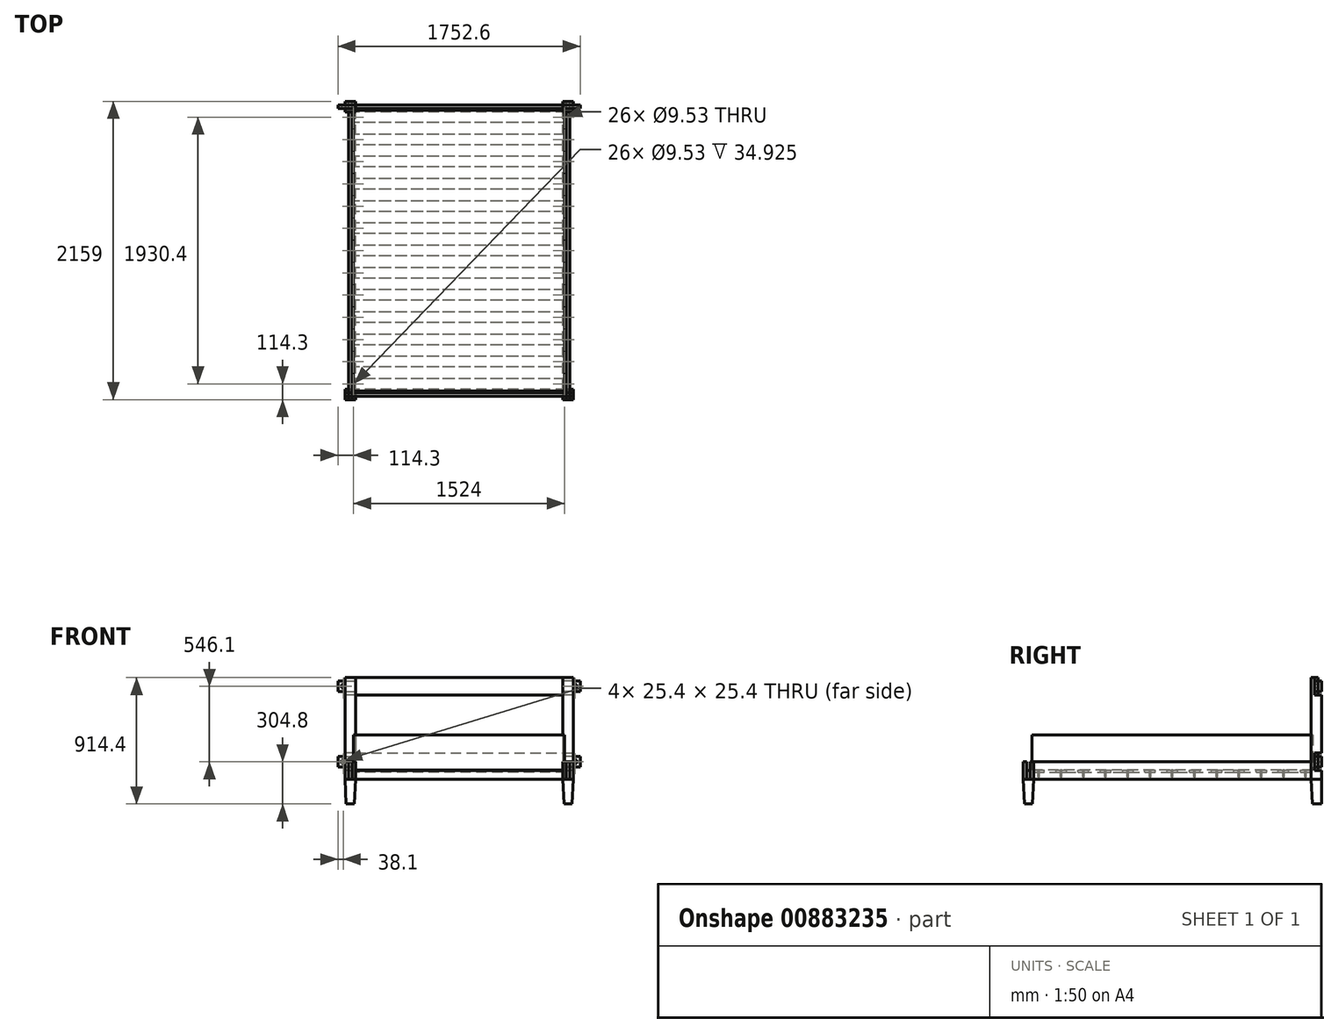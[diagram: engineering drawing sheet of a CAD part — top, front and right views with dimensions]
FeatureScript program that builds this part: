
annotation { "Feature Type Name" : "Feature", "Feature Type Description" : "" }
export const myFeature = defineFeature(function(context is Context, id is Id, definition is map)
    precondition{}
    {
        {
            var Q0;
            Q0=qCreatedBy(makeId("Top.planeOp"),FACE);
            var sketch = newSketch(context, id + "F0", { "sketchPlane" : qUnion([Q0])});
            skLineSegment(sketch, "E0.bottom", {"start": v(0, 0) * mm, "end": v(76.2, 0) * mm});
            skLineSegment(sketch, "E0.top", {"start": v(0, 76.2) * mm, "end": v(76.2, 76.2) * mm});
            skLineSegment(sketch, "E0.left", {"start": v(0, 0) * mm, "end": v(0, 76.2) * mm});
            skLineSegment(sketch, "E0.right", {"start": v(76.2, 0) * mm, "end": v(76.2, 76.2) * mm});
            skLineSegment(sketch, "E1.bottom", {"start": v(1574.8, 0) * mm, "end": v(1651, 0) * mm});
            skLineSegment(sketch, "E1.top", {"start": v(1574.8, 76.2) * mm, "end": v(1651, 76.2) * mm});
            skLineSegment(sketch, "E1.left", {"start": v(1574.8, 0) * mm, "end": v(1574.8, 76.2) * mm});
            skLineSegment(sketch, "E1.right", {"start": v(1651, 0) * mm, "end": v(1651, 76.2) * mm});
            skLineSegment(sketch, "E2.bottom", {"start": v(0, 2082.8) * mm, "end": v(76.2, 2082.8) * mm});
            skLineSegment(sketch, "E2.top", {"start": v(0, 2159) * mm, "end": v(76.2, 2159) * mm});
            skLineSegment(sketch, "E2.left", {"start": v(0, 2082.8) * mm, "end": v(0, 2159) * mm});
            skLineSegment(sketch, "E2.right", {"start": v(76.2, 2082.8) * mm, "end": v(76.2, 2159) * mm});
            skLineSegment(sketch, "E3.bottom", {"start": v(1574.8, 2082.8) * mm, "end": v(1651, 2082.8) * mm});
            skLineSegment(sketch, "E3.top", {"start": v(1574.8, 2159) * mm, "end": v(1651, 2159) * mm});
            skLineSegment(sketch, "E3.left", {"start": v(1574.8, 2082.8) * mm, "end": v(1574.8, 2159) * mm});
            skLineSegment(sketch, "E3.right", {"start": v(1651, 2082.8) * mm, "end": v(1651, 2159) * mm});
            skSolve(sketch);
        }
        {
            var Q0;
            Q0 = qSketchRegion(id + "F0", true);
            extrude(context, id + "F1", {"entities" : qUnion([Q0]), "depth" : 304.8 * mm, "offsetDistance" : 25.4 * mm});
        }
        {
            var Q0;
            Q0=makeQuery(id+"F1.opExtrude","CAP_FACE",FACE,{"disambiguationData":[OSD([sQuery(id+"F0.wireOp",EDGE,"E2.bottom"),sQuery(id+"F0.wireOp",EDGE,"E2.top"),sQuery(id+"F0.wireOp",EDGE,"E2.left"),sQuery(id+"F0.wireOp",EDGE,"E2.right")])],"isStart":false});
            var Q1;
            Q1=makeQuery(id+"F1.opExtrude","CAP_FACE",FACE,{"disambiguationData":[OSD([sQuery(id+"F0.wireOp",EDGE,"E3.bottom"),sQuery(id+"F0.wireOp",EDGE,"E3.top"),sQuery(id+"F0.wireOp",EDGE,"E3.left"),sQuery(id+"F0.wireOp",EDGE,"E3.right")])],"isStart":false});
            extrude(context, id + "F2", {"entities" : qUnion([Q0, Q1]), "operationType" : NewBodyOperationType.ADD, "depth" : 609.6 * mm, "offsetDistance" : 25.4 * mm});
        }
        {
            var Q0;
            {var subQ0=sQuery(id+"F0.wireOp",EDGE,"E2.top");Q0=makeQuery(id+"F2.boolean.opBoolean","MERGE",FACE,{"derivedFrom":[makeQuery(id+"F1.opExtrude","SWEPT_FACE",FACE,{"disambiguationData":[OSD([subQ0])]}),makeQuery(id+"F2.opExtrude","SWEPT_FACE",FACE,{"disambiguationData":[OSD([subQ0])]})]});}
            var sketch = newSketch(context, id + "F3", { "sketchPlane" : qUnion([Q0])});
            skLineSegment(sketch, "E4.bottom", {"start": v(-25.4, 304.8) * mm, "end": v(-50.8, 304.8) * mm});
            skLineSegment(sketch, "E4.top", {"start": v(-50.8, 177.8) * mm, "end": v(-25.4, 177.8) * mm});
            skLineSegment(sketch, "E4.left", {"start": v(-25.4, 304.8) * mm, "end": v(-25.4, 177.8) * mm});
            skLineSegment(sketch, "E4.right", {"start": v(-50.8, 304.8) * mm, "end": v(-50.8, 177.8) * mm});
            skLineSegment(sketch, "E5", {"start": v(-38.1, 177.8) * mm, "end": v(-38.1, 0) * mm, "construction": true});
            skPoint(sketch, "E5.endSnap0", {"position": v(-38.1, 0) * mm});
            skLineSegment(sketch, "E6.bottom", {"start": v(-1625.6, 304.8) * mm, "end": v(-1600.2, 304.8) * mm});
            skLineSegment(sketch, "E6.top", {"start": v(-1625.6, 177.8) * mm, "end": v(-1600.2, 177.8) * mm});
            skLineSegment(sketch, "E6.left", {"start": v(-1625.6, 304.8) * mm, "end": v(-1625.6, 177.8) * mm});
            skLineSegment(sketch, "E6.right", {"start": v(-1600.2, 304.8) * mm, "end": v(-1600.2, 177.8) * mm});
            skLineSegment(sketch, "E7", {"start": v(-1612.9, 177.8) * mm, "end": v(-1612.9, 0) * mm, "construction": true});
            skSolve(sketch);
        }
        {
            var Q0;
            Q0 = qSketchRegion(id + "F3", true);
            var Q1;
            Q1=makeQuery(id+"F1.opExtrude","SWEPT_FACE",FACE,{"disambiguationData":[OSD([sQuery(id+"F0.wireOp",EDGE,"E0.bottom")])]});
            extrude(context, id + "F4", {"entities" : qUnion([Q0]), "endBound" : BoundingType.UP_TO_SURFACE, "oppositeDirection" : true, "depth" : 25.4 * mm, "endBoundEntityFace" : qUnion([Q1]), "offsetDistance" : 25.4 * mm});
        }
        {
            var Q0;
            Q0=makeQuery(id+"F4.opExtrude","SWEPT_BODY",BODY,{"disambiguationData":[OSD([sQuery(id+"F3.wireOp",EDGE,"E4.bottom"),sQuery(id+"F3.wireOp",EDGE,"E4.top"),sQuery(id+"F3.wireOp",EDGE,"E4.left"),sQuery(id+"F3.wireOp",EDGE,"E4.right")])]});
            var Q1;
            Q1=makeQuery(id+"F4.opExtrude","SWEPT_BODY",BODY,{"disambiguationData":[OSD([sQuery(id+"F3.wireOp",EDGE,"E6.bottom"),sQuery(id+"F3.wireOp",EDGE,"E6.top"),sQuery(id+"F3.wireOp",EDGE,"E6.left"),sQuery(id+"F3.wireOp",EDGE,"E6.right")])]});
            var Q2;
            Q2=makeQuery(id+"F1.opExtrude","SWEPT_BODY",BODY,{"disambiguationData":[OSD([sQuery(id+"F0.wireOp",EDGE,"E0.bottom"),sQuery(id+"F0.wireOp",EDGE,"E0.top"),sQuery(id+"F0.wireOp",EDGE,"E0.left"),sQuery(id+"F0.wireOp",EDGE,"E0.right")])]});
            var Q3;
            Q3=makeQuery(id+"F1.opExtrude","SWEPT_BODY",BODY,{"disambiguationData":[OSD([sQuery(id+"F0.wireOp",EDGE,"E1.bottom"),sQuery(id+"F0.wireOp",EDGE,"E1.top"),sQuery(id+"F0.wireOp",EDGE,"E1.left"),sQuery(id+"F0.wireOp",EDGE,"E1.right")])]});
            booleanBodies(context, id + "F5", {"operationType" : BooleanOperationType.SUBTRACTION, "tools" : qUnion([Q0, Q1]), "targets" : qUnion([Q2, Q3]), "keepTools" : true});
        }
        {
            var Q0;
            Q0=makeQuery(id+"F1.opExtrude","SWEPT_FACE",FACE,{"disambiguationData":[OSD([sQuery(id+"F0.wireOp",EDGE,"E1.right")])]});
            var sketch = newSketch(context, id + "F6", { "sketchPlane" : qUnion([Q0])});
            skLineSegment(sketch, "E8.bottom", {"start": v(25.4, 304.8) * mm, "end": v(50.8, 304.8) * mm});
            skLineSegment(sketch, "E8.top", {"start": v(25.4, 177.8) * mm, "end": v(50.8, 177.8) * mm});
            skLineSegment(sketch, "E8.left", {"start": v(25.4, 304.8) * mm, "end": v(25.4, 177.8) * mm});
            skLineSegment(sketch, "E8.right", {"start": v(50.8, 304.8) * mm, "end": v(50.8, 177.8) * mm});
            skLineSegment(sketch, "E9", {"start": v(0, 304.8) * mm, "end": v(25.4, 304.8) * mm, "construction": true});
            skLineSegment(sketch, "E10", {"start": v(76.2, 304.8) * mm, "end": v(50.8, 304.8) * mm, "construction": true});
            skSolve(sketch);
        }
        {
            var Q0;
            Q0 = qSketchRegion(id + "F6", true);
            var Q1;
            Q1=makeQuery(id+"F1.opExtrude","SWEPT_FACE",FACE,{"disambiguationData":[OSD([sQuery(id+"F0.wireOp",EDGE,"E0.left")])]});
            extrude(context, id + "F7", {"entities" : qUnion([Q0]), "endBound" : BoundingType.UP_TO_SURFACE, "oppositeDirection" : true, "depth" : 25.4 * mm, "endBoundEntityFace" : qUnion([Q1]), "offsetDistance" : 25.4 * mm});
        }
        {
            var Q0;
            Q0=makeQuery(id+"F7.opExtrude","SWEPT_BODY",BODY,{"disambiguationData":[OSD([sQuery(id+"F6.wireOp",EDGE,"E8.bottom"),sQuery(id+"F6.wireOp",EDGE,"E8.top"),sQuery(id+"F6.wireOp",EDGE,"E8.left"),sQuery(id+"F6.wireOp",EDGE,"E8.right")])]});
            var Q1;
            Q1=makeQuery(id+"F1.opExtrude","SWEPT_BODY",BODY,{"disambiguationData":[OSD([sQuery(id+"F0.wireOp",EDGE,"E0.bottom"),sQuery(id+"F0.wireOp",EDGE,"E0.top"),sQuery(id+"F0.wireOp",EDGE,"E0.left"),sQuery(id+"F0.wireOp",EDGE,"E0.right")])]});
            var Q2;
            Q2=makeQuery(id+"F1.opExtrude","SWEPT_BODY",BODY,{"disambiguationData":[OSD([sQuery(id+"F0.wireOp",EDGE,"E1.bottom"),sQuery(id+"F0.wireOp",EDGE,"E1.top"),sQuery(id+"F0.wireOp",EDGE,"E1.left"),sQuery(id+"F0.wireOp",EDGE,"E1.right")])]});
            booleanBodies(context, id + "F8", {"operationType" : BooleanOperationType.SUBTRACTION, "tools" : qUnion([Q0]), "targets" : qUnion([Q1, Q2]), "keepTools" : true});
        }
        {
            var Q0;
            Q0=makeQuery(id+"F7.opExtrude","CAP_FACE",FACE,{"disambiguationData":[OSD([sQuery(id+"F6.wireOp",EDGE,"E8.bottom"),sQuery(id+"F6.wireOp",EDGE,"E8.top"),sQuery(id+"F6.wireOp",EDGE,"E8.left"),sQuery(id+"F6.wireOp",EDGE,"E8.right")])],"isStart":false});
            var sketch = newSketch(context, id + "F9", { "sketchPlane" : qUnion([Q0])});
            skLineSegment(sketch, "E11.bottom", {"start": v(-50.8, 304.8) * mm, "end": v(-25.4, 304.8) * mm});
            skLineSegment(sketch, "E11.top", {"start": v(-50.8, 241.3) * mm, "end": v(-25.4, 241.3) * mm});
            skLineSegment(sketch, "E11.left", {"start": v(-50.8, 304.8) * mm, "end": v(-50.8, 241.3) * mm});
            skLineSegment(sketch, "E11.right", {"start": v(-25.4, 304.8) * mm, "end": v(-25.4, 241.3) * mm});
            skSolve(sketch);
        }
        {
            var Q0;
            Q0 = qSketchRegion(id + "F9", true);
            extrude(context, id + "F10", {"entities" : qUnion([Q0]), "operationType" : NewBodyOperationType.REMOVE, "endBound" : BoundingType.THROUGH_ALL, "oppositeDirection" : true, "depth" : 25.4 * mm, "offsetDistance" : 25.4 * mm});
        }
        {
            var Q0;
            Q0=makeQuery(id+"F4.opExtrude","SWEPT_BODY",BODY,{"disambiguationData":[OSD([sQuery(id+"F3.wireOp",EDGE,"E4.bottom"),sQuery(id+"F3.wireOp",EDGE,"E4.top"),sQuery(id+"F3.wireOp",EDGE,"E4.left"),sQuery(id+"F3.wireOp",EDGE,"E4.right")])]});
            var Q1;
            Q1=makeQuery(id+"F4.opExtrude","SWEPT_BODY",BODY,{"disambiguationData":[OSD([sQuery(id+"F3.wireOp",EDGE,"E6.bottom"),sQuery(id+"F3.wireOp",EDGE,"E6.top"),sQuery(id+"F3.wireOp",EDGE,"E6.left"),sQuery(id+"F3.wireOp",EDGE,"E6.right")])]});
            var Q2;
            Q2=makeQuery(id+"F7.opExtrude","SWEPT_BODY",BODY,{"disambiguationData":[OSD([sQuery(id+"F6.wireOp",EDGE,"E8.bottom"),sQuery(id+"F6.wireOp",EDGE,"E8.top"),sQuery(id+"F6.wireOp",EDGE,"E8.left"),sQuery(id+"F6.wireOp",EDGE,"E8.right")])]});
            booleanBodies(context, id + "F11", {"operationType" : BooleanOperationType.SUBTRACTION, "tools" : qUnion([Q0, Q1]), "targets" : qUnion([Q2]), "keepTools" : true});
        }
        {
            var Q0;
            Q0=makeQuery(id+"F4.opExtrude","SWEPT_BODY",BODY,{"disambiguationData":[OSD([sQuery(id+"F3.wireOp",EDGE,"E4.bottom"),sQuery(id+"F3.wireOp",EDGE,"E4.top"),sQuery(id+"F3.wireOp",EDGE,"E4.left"),sQuery(id+"F3.wireOp",EDGE,"E4.right")])]});
            var Q1;
            Q1=makeQuery(id+"F4.opExtrude","SWEPT_BODY",BODY,{"disambiguationData":[OSD([sQuery(id+"F3.wireOp",EDGE,"E6.bottom"),sQuery(id+"F3.wireOp",EDGE,"E6.top"),sQuery(id+"F3.wireOp",EDGE,"E6.left"),sQuery(id+"F3.wireOp",EDGE,"E6.right")])]});
            var Q2;
            Q2=makeQuery(id+"F1.opExtrude","SWEPT_BODY",BODY,{"disambiguationData":[OSD([sQuery(id+"F0.wireOp",EDGE,"E2.bottom"),sQuery(id+"F0.wireOp",EDGE,"E2.top"),sQuery(id+"F0.wireOp",EDGE,"E2.left"),sQuery(id+"F0.wireOp",EDGE,"E2.right")])]});
            var Q3;
            Q3=makeQuery(id+"F1.opExtrude","SWEPT_BODY",BODY,{"disambiguationData":[OSD([sQuery(id+"F0.wireOp",EDGE,"E3.bottom"),sQuery(id+"F0.wireOp",EDGE,"E3.top"),sQuery(id+"F0.wireOp",EDGE,"E3.left"),sQuery(id+"F0.wireOp",EDGE,"E3.right")])]});
            booleanBodies(context, id + "F12", {"operationType" : BooleanOperationType.SUBTRACTION, "tools" : qUnion([Q0, Q1]), "targets" : qUnion([Q2, Q3]), "keepTools" : true});
        }
        {
            var Q0;
            {var subQ0=sQuery(id+"F0.wireOp",EDGE,"E2.left");Q0=makeQuery(id+"F2.boolean.opBoolean","MERGE",FACE,{"derivedFrom":[makeQuery(id+"F1.opExtrude","SWEPT_FACE",FACE,{"disambiguationData":[OSD([subQ0])]}),makeQuery(id+"F2.opExtrude","SWEPT_FACE",FACE,{"disambiguationData":[OSD([subQ0])]})]});}
            var sketch = newSketch(context, id + "F13", { "sketchPlane" : qUnion([Q0])});
            skLineSegment(sketch, "E12.bottom", {"start": v(-2133.6, 368.3) * mm, "end": v(-2108.2, 368.3) * mm});
            skLineSegment(sketch, "E12.top", {"start": v(-2133.6, 241.3) * mm, "end": v(-2108.2, 241.3) * mm});
            skLineSegment(sketch, "E12.left", {"start": v(-2133.6, 368.3) * mm, "end": v(-2133.6, 241.3) * mm});
            skLineSegment(sketch, "E12.right", {"start": v(-2108.2, 368.3) * mm, "end": v(-2108.2, 241.3) * mm});
            skLineSegment(sketch, "E13", {"start": v(-2159, 241.3) * mm, "end": v(-2133.6, 241.3) * mm});
            skLineSegment(sketch, "E14", {"start": v(-2082.8, 241.3) * mm, "end": v(-2108.2, 241.3) * mm});
            skLineSegment(sketch, "E15.bottom", {"start": v(-2133.6, 914.4) * mm, "end": v(-2108.2, 914.4) * mm});
            skLineSegment(sketch, "E15.top", {"start": v(-2133.6, 787.4) * mm, "end": v(-2108.2, 787.4) * mm});
            skLineSegment(sketch, "E15.left", {"start": v(-2133.6, 914.4) * mm, "end": v(-2133.6, 787.4) * mm});
            skLineSegment(sketch, "E15.right", {"start": v(-2108.2, 914.4) * mm, "end": v(-2108.2, 787.4) * mm});
            skSolve(sketch);
        }
        {
            var Q0;
            Q0 = qSketchRegion(id + "F13", true);
            extrude(context, id + "F14", {"entities" : qUnion([Q0]), "depth" : 50.8 * mm, "offsetDistance" : 25.4 * mm, "hasSecondDirection" : true, "secondDirectionOppositeDirection" : true, "secondDirectionDepth" : 1701.8 * mm});
        }
        {
            var Q0;
            Q0=makeQuery(id+"F14.opExtrude","SWEPT_FACE",FACE,{"disambiguationData":[OSD([sQuery(id+"F13.wireOp",EDGE,"E15.right")])]});
            var sketch = newSketch(context, id + "F15", { "sketchPlane" : qUnion([Q0])});
            skLineSegment(sketch, "E16.bottom", {"start": v(-50.8, 914.4) * mm, "end": v(76.2, 914.4) * mm});
            skLineSegment(sketch, "E16.top", {"start": v(-50.8, 889) * mm, "end": v(76.2, 889) * mm});
            skLineSegment(sketch, "E16.left", {"start": v(-50.8, 914.4) * mm, "end": v(-50.8, 889) * mm});
            skLineSegment(sketch, "E16.right", {"start": v(76.2, 914.4) * mm, "end": v(76.2, 889) * mm});
            skLineSegment(sketch, "E17.bottom", {"start": v(-50.8, 787.4) * mm, "end": v(76.2, 787.4) * mm});
            skLineSegment(sketch, "E17.top", {"start": v(-50.8, 812.8) * mm, "end": v(76.2, 812.8) * mm});
            skLineSegment(sketch, "E17.left", {"start": v(-50.8, 787.4) * mm, "end": v(-50.8, 812.8) * mm});
            skLineSegment(sketch, "E17.right", {"start": v(76.2, 787.4) * mm, "end": v(76.2, 812.8) * mm});
            skLineSegment(sketch, "E18.bottom", {"start": v(-50.8, 368.3) * mm, "end": v(76.2, 368.3) * mm});
            skLineSegment(sketch, "E18.top", {"start": v(-50.8, 342.9) * mm, "end": v(76.2, 342.9) * mm});
            skLineSegment(sketch, "E18.left", {"start": v(-50.8, 368.3) * mm, "end": v(-50.8, 342.9) * mm});
            skLineSegment(sketch, "E18.right", {"start": v(76.2, 368.3) * mm, "end": v(76.2, 342.9) * mm});
            skLineSegment(sketch, "E19.bottom", {"start": v(76.2, 241.3) * mm, "end": v(-50.8, 241.3) * mm});
            skLineSegment(sketch, "E19.top", {"start": v(76.2, 266.7) * mm, "end": v(-50.8, 266.7) * mm});
            skLineSegment(sketch, "E19.left", {"start": v(76.2, 241.3) * mm, "end": v(76.2, 266.7) * mm});
            skLineSegment(sketch, "E19.right", {"start": v(-50.8, 241.3) * mm, "end": v(-50.8, 266.7) * mm});
            skLineSegment(sketch, "E20.bottom", {"start": v(1701.8, 368.3) * mm, "end": v(1574.8, 368.3) * mm});
            skLineSegment(sketch, "E20.top", {"start": v(1701.8, 342.9) * mm, "end": v(1574.8, 342.9) * mm});
            skLineSegment(sketch, "E20.left", {"start": v(1701.8, 368.3) * mm, "end": v(1701.8, 342.9) * mm});
            skLineSegment(sketch, "E20.right", {"start": v(1574.8, 368.3) * mm, "end": v(1574.8, 342.9) * mm});
            skLineSegment(sketch, "E21.bottom", {"start": v(1701.8, 241.3) * mm, "end": v(1574.8, 241.3) * mm});
            skLineSegment(sketch, "E21.top", {"start": v(1701.8, 266.7) * mm, "end": v(1574.8, 266.7) * mm});
            skLineSegment(sketch, "E21.left", {"start": v(1701.8, 241.3) * mm, "end": v(1701.8, 266.7) * mm});
            skLineSegment(sketch, "E21.right", {"start": v(1574.8, 241.3) * mm, "end": v(1574.8, 266.7) * mm});
            skLineSegment(sketch, "E22.bottom", {"start": v(1701.8, 914.4) * mm, "end": v(1574.8, 914.4) * mm});
            skLineSegment(sketch, "E22.top", {"start": v(1701.8, 889) * mm, "end": v(1574.8, 889) * mm});
            skLineSegment(sketch, "E22.left", {"start": v(1701.8, 914.4) * mm, "end": v(1701.8, 889) * mm});
            skLineSegment(sketch, "E22.right", {"start": v(1574.8, 914.4) * mm, "end": v(1574.8, 889) * mm});
            skLineSegment(sketch, "E23.bottom", {"start": v(1701.8, 787.4) * mm, "end": v(1574.8, 787.4) * mm});
            skLineSegment(sketch, "E23.top", {"start": v(1701.8, 812.8) * mm, "end": v(1574.8, 812.8) * mm});
            skLineSegment(sketch, "E23.left", {"start": v(1701.8, 787.4) * mm, "end": v(1701.8, 812.8) * mm});
            skLineSegment(sketch, "E23.right", {"start": v(1574.8, 787.4) * mm, "end": v(1574.8, 812.8) * mm});
            skLineSegment(sketch, "E24.bottom", {"start": v(0, 838.2) * mm, "end": v(-25.4, 838.2) * mm});
            skLineSegment(sketch, "E24.top", {"start": v(0, 863.6) * mm, "end": v(-25.4, 863.6) * mm});
            skLineSegment(sketch, "E24.left", {"start": v(0, 838.2) * mm, "end": v(0, 863.6) * mm});
            skLineSegment(sketch, "E24.right", {"start": v(-25.4, 838.2) * mm, "end": v(-25.4, 863.6) * mm});
            skLineSegment(sketch, "E25", {"start": v(-50.8, 850.9) * mm, "end": v(-25.4, 850.9) * mm, "construction": true});
            skLineSegment(sketch, "E26.bottom", {"start": v(0, 292.1) * mm, "end": v(-25.4, 292.1) * mm});
            skLineSegment(sketch, "E26.top", {"start": v(0, 317.5) * mm, "end": v(-25.4, 317.5) * mm});
            skLineSegment(sketch, "E26.left", {"start": v(0, 292.1) * mm, "end": v(0, 317.5) * mm});
            skLineSegment(sketch, "E26.right", {"start": v(-25.4, 292.1) * mm, "end": v(-25.4, 317.5) * mm});
            skLineSegment(sketch, "E27", {"start": v(-50.8, 304.8) * mm, "end": v(-25.4, 304.8) * mm, "construction": true});
            skLineSegment(sketch, "E28.bottom", {"start": v(1651, 292.1) * mm, "end": v(1676.4, 292.1) * mm});
            skLineSegment(sketch, "E28.top", {"start": v(1651, 317.5) * mm, "end": v(1676.4, 317.5) * mm});
            skLineSegment(sketch, "E28.left", {"start": v(1651, 292.1) * mm, "end": v(1651, 317.5) * mm});
            skLineSegment(sketch, "E28.right", {"start": v(1676.4, 292.1) * mm, "end": v(1676.4, 317.5) * mm});
            skLineSegment(sketch, "E29", {"start": v(1676.4, 304.8) * mm, "end": v(1701.8, 304.8) * mm, "construction": true});
            skLineSegment(sketch, "E30.bottom", {"start": v(1651, 863.6) * mm, "end": v(1676.4, 863.6) * mm});
            skLineSegment(sketch, "E30.top", {"start": v(1651, 838.2) * mm, "end": v(1676.4, 838.2) * mm});
            skLineSegment(sketch, "E30.left", {"start": v(1651, 863.6) * mm, "end": v(1651, 838.2) * mm});
            skLineSegment(sketch, "E30.right", {"start": v(1676.4, 863.6) * mm, "end": v(1676.4, 838.2) * mm});
            skLineSegment(sketch, "E31", {"start": v(1676.4, 850.9) * mm, "end": v(1701.8, 850.9) * mm, "construction": true});
            skSolve(sketch);
        }
        {
            var Q0;
            Q0 = qSketchRegion(id + "F15", true);
            extrude(context, id + "F16", {"entities" : qUnion([Q0]), "operationType" : NewBodyOperationType.REMOVE, "endBound" : BoundingType.THROUGH_ALL, "oppositeDirection" : true, "depth" : 25.4 * mm, "offsetDistance" : 25.4 * mm});
        }
        {
            var Q0;
            Q0=makeQuery(id+"F14.opExtrude","SWEPT_BODY",BODY,{"disambiguationData":[OSD([sQuery(id+"F13.wireOp",EDGE,"E15.bottom"),sQuery(id+"F13.wireOp",EDGE,"E15.top"),sQuery(id+"F13.wireOp",EDGE,"E15.left"),sQuery(id+"F13.wireOp",EDGE,"E15.right")])]});
            var Q1;
            Q1=makeQuery(id+"F14.opExtrude","SWEPT_BODY",BODY,{"disambiguationData":[OSD([sQuery(id+"F13.wireOp",EDGE,"E12.bottom"),sQuery(id+"F13.wireOp",EDGE,"E12.top"),sQuery(id+"F13.wireOp",EDGE,"E12.left"),sQuery(id+"F13.wireOp",EDGE,"E12.right")])]});
            var Q2;
            Q2=makeQuery(id+"F1.opExtrude","SWEPT_BODY",BODY,{"disambiguationData":[OSD([sQuery(id+"F0.wireOp",EDGE,"E2.bottom"),sQuery(id+"F0.wireOp",EDGE,"E2.top"),sQuery(id+"F0.wireOp",EDGE,"E2.left"),sQuery(id+"F0.wireOp",EDGE,"E2.right")])]});
            var Q3;
            Q3=makeQuery(id+"F4.opExtrude","SWEPT_BODY",BODY,{"disambiguationData":[OSD([sQuery(id+"F3.wireOp",EDGE,"E4.bottom"),sQuery(id+"F3.wireOp",EDGE,"E4.top"),sQuery(id+"F3.wireOp",EDGE,"E4.left"),sQuery(id+"F3.wireOp",EDGE,"E4.right")])]});
            var Q4;
            Q4=makeQuery(id+"F4.opExtrude","SWEPT_BODY",BODY,{"disambiguationData":[OSD([sQuery(id+"F3.wireOp",EDGE,"E6.bottom"),sQuery(id+"F3.wireOp",EDGE,"E6.top"),sQuery(id+"F3.wireOp",EDGE,"E6.left"),sQuery(id+"F3.wireOp",EDGE,"E6.right")])]});
            var Q5;
            Q5=makeQuery(id+"F1.opExtrude","SWEPT_BODY",BODY,{"disambiguationData":[OSD([sQuery(id+"F0.wireOp",EDGE,"E3.bottom"),sQuery(id+"F0.wireOp",EDGE,"E3.top"),sQuery(id+"F0.wireOp",EDGE,"E3.left"),sQuery(id+"F0.wireOp",EDGE,"E3.right")])]});
            booleanBodies(context, id + "F17", {"operationType" : BooleanOperationType.SUBTRACTION, "tools" : qUnion([Q0, Q1]), "targets" : qUnion([Q2, Q3, Q4, Q5]), "keepTools" : true});
        }
        {
            var Q0;
            {var subQ0=sQuery(id+"F0.wireOp",EDGE,"E2.bottom");Q0=makeQuery(id+"F2.boolean.opBoolean","MERGE",FACE,{"derivedFrom":[makeQuery(id+"F1.opExtrude","SWEPT_FACE",FACE,{"disambiguationData":[OSD([subQ0])]}),makeQuery(id+"F2.opExtrude","SWEPT_FACE",FACE,{"disambiguationData":[OSD([subQ0])]})]});}
            var sketch = newSketch(context, id + "F18", { "sketchPlane" : qUnion([Q0])});
            skLineSegment(sketch, "E32.bottom", {"start": v(50.8, 177.8) * mm, "end": v(76.2, 177.8) * mm});
            skLineSegment(sketch, "E32.top", {"start": v(50.8, 228.6) * mm, "end": v(76.2, 228.6) * mm});
            skLineSegment(sketch, "E32.left", {"start": v(50.8, 177.8) * mm, "end": v(50.8, 228.6) * mm});
            skLineSegment(sketch, "E32.right", {"start": v(76.2, 177.8) * mm, "end": v(76.2, 228.6) * mm});
            skLineSegment(sketch, "E33.bottom", {"start": v(1600.2, 177.8) * mm, "end": v(1574.8, 177.8) * mm});
            skLineSegment(sketch, "E33.top", {"start": v(1600.2, 228.6) * mm, "end": v(1574.8, 228.6) * mm});
            skLineSegment(sketch, "E33.left", {"start": v(1600.2, 177.8) * mm, "end": v(1600.2, 228.6) * mm});
            skLineSegment(sketch, "E33.right", {"start": v(1574.8, 177.8) * mm, "end": v(1574.8, 228.6) * mm});
            skSolve(sketch);
        }
        {
            var Q0;
            Q0 = qSketchRegion(id + "F18", true);
            var Q1;
            Q1=makeQuery(id+"F1.opExtrude","SWEPT_FACE",FACE,{"disambiguationData":[OSD([sQuery(id+"F0.wireOp",EDGE,"E0.top")])]});
            extrude(context, id + "F19", {"entities" : qUnion([Q0]), "endBound" : BoundingType.UP_TO_SURFACE, "depth" : 25.4 * mm, "endBoundEntityFace" : qUnion([Q1]), "offsetDistance" : 25.4 * mm});
        }
        {
            var Q0;
            Q0=makeQuery(id+"F4.opExtrude","SWEPT_FACE",FACE,{"disambiguationData":[OSD([sQuery(id+"F3.wireOp",EDGE,"E4.right")])]});
            var sketch = newSketch(context, id + "F20", { "sketchPlane" : qUnion([Q0])});
            skLineSegment(sketch, "E34.bottom", {"start": v(76.2, 228.6) * mm, "end": v(152.4, 228.6) * mm});
            skLineSegment(sketch, "E34.top", {"start": v(76.2, 244.47) * mm, "end": v(152.4, 244.47) * mm});
            skLineSegment(sketch, "E34.left", {"start": v(76.2, 228.6) * mm, "end": v(76.2, 244.47) * mm});
            skLineSegment(sketch, "E34.right", {"start": v(152.4, 228.6) * mm, "end": v(152.4, 244.47) * mm});
            skLineSegment(sketch, "E35.1.0.0", {"start": v(237.07, 228.6) * mm, "end": v(237.07, 244.47) * mm});
            skLineSegment(sketch, "E35.1.0.1", {"start": v(237.07, 228.6) * mm, "end": v(313.27, 228.6) * mm});
            skLineSegment(sketch, "E35.1.0.2", {"start": v(237.07, 244.47) * mm, "end": v(313.27, 244.47) * mm});
            skLineSegment(sketch, "E35.1.0.3", {"start": v(313.27, 228.6) * mm, "end": v(313.27, 244.47) * mm});
            skLineSegment(sketch, "E35.2.0.0", {"start": v(397.93, 228.6) * mm, "end": v(397.93, 244.47) * mm});
            skLineSegment(sketch, "E35.2.0.1", {"start": v(397.93, 228.6) * mm, "end": v(474.13, 228.6) * mm});
            skLineSegment(sketch, "E35.2.0.2", {"start": v(397.93, 244.47) * mm, "end": v(474.13, 244.47) * mm});
            skLineSegment(sketch, "E35.2.0.3", {"start": v(474.13, 228.6) * mm, "end": v(474.13, 244.47) * mm});
            skLineSegment(sketch, "E35.direction1", {"start": v(76.2, 228.6) * mm, "end": v(237.07, 228.6) * mm, "construction": true});
            skLineSegment(sketch, "E36.0.3.0", {"start": v(558.8, 228.6) * mm, "end": v(558.8, 244.47) * mm});
            skLineSegment(sketch, "E36.3.3.0", {"start": v(558.8, 228.6) * mm, "end": v(635, 228.6) * mm});
            skLineSegment(sketch, "E36.6.3.0", {"start": v(558.8, 244.47) * mm, "end": v(635, 244.47) * mm});
            skLineSegment(sketch, "E36.9.3.0", {"start": v(635, 228.6) * mm, "end": v(635, 244.47) * mm});
            skLineSegment(sketch, "E36.0.4.0", {"start": v(719.67, 228.6) * mm, "end": v(719.67, 244.47) * mm});
            skLineSegment(sketch, "E36.3.4.0", {"start": v(719.67, 228.6) * mm, "end": v(795.87, 228.6) * mm});
            skLineSegment(sketch, "E36.6.4.0", {"start": v(719.67, 244.47) * mm, "end": v(795.87, 244.47) * mm});
            skLineSegment(sketch, "E36.9.4.0", {"start": v(795.87, 228.6) * mm, "end": v(795.87, 244.47) * mm});
            skLineSegment(sketch, "E36.0.5.0", {"start": v(880.53, 228.6) * mm, "end": v(880.53, 244.47) * mm});
            skLineSegment(sketch, "E36.3.5.0", {"start": v(880.53, 228.6) * mm, "end": v(956.73, 228.6) * mm});
            skLineSegment(sketch, "E36.6.5.0", {"start": v(880.53, 244.47) * mm, "end": v(956.73, 244.47) * mm});
            skLineSegment(sketch, "E36.9.5.0", {"start": v(956.73, 228.6) * mm, "end": v(956.73, 244.47) * mm});
            skLineSegment(sketch, "E36.0.6.0", {"start": v(1041.4, 228.6) * mm, "end": v(1041.4, 244.47) * mm});
            skLineSegment(sketch, "E36.3.6.0", {"start": v(1041.4, 228.6) * mm, "end": v(1117.6, 228.6) * mm});
            skLineSegment(sketch, "E36.6.6.0", {"start": v(1041.4, 244.47) * mm, "end": v(1117.6, 244.47) * mm});
            skLineSegment(sketch, "E36.9.6.0", {"start": v(1117.6, 228.6) * mm, "end": v(1117.6, 244.47) * mm});
            skLineSegment(sketch, "E36.0.7.0", {"start": v(1202.27, 228.6) * mm, "end": v(1202.27, 244.47) * mm});
            skLineSegment(sketch, "E36.3.7.0", {"start": v(1202.27, 228.6) * mm, "end": v(1278.47, 228.6) * mm});
            skLineSegment(sketch, "E36.6.7.0", {"start": v(1202.27, 244.47) * mm, "end": v(1278.47, 244.47) * mm});
            skLineSegment(sketch, "E36.9.7.0", {"start": v(1278.47, 228.6) * mm, "end": v(1278.47, 244.47) * mm});
            skLineSegment(sketch, "E36.0.8.0", {"start": v(1363.13, 228.6) * mm, "end": v(1363.13, 244.47) * mm});
            skLineSegment(sketch, "E36.3.8.0", {"start": v(1363.13, 228.6) * mm, "end": v(1439.33, 228.6) * mm});
            skLineSegment(sketch, "E36.6.8.0", {"start": v(1363.13, 244.47) * mm, "end": v(1439.33, 244.47) * mm});
            skLineSegment(sketch, "E36.9.8.0", {"start": v(1439.33, 228.6) * mm, "end": v(1439.33, 244.47) * mm});
            skLineSegment(sketch, "E36.0.9.0", {"start": v(1524, 228.6) * mm, "end": v(1524, 244.47) * mm});
            skLineSegment(sketch, "E36.3.9.0", {"start": v(1524, 228.6) * mm, "end": v(1600.2, 228.6) * mm});
            skLineSegment(sketch, "E36.6.9.0", {"start": v(1524, 244.47) * mm, "end": v(1600.2, 244.47) * mm});
            skLineSegment(sketch, "E36.9.9.0", {"start": v(1600.2, 228.6) * mm, "end": v(1600.2, 244.47) * mm});
            skLineSegment(sketch, "E36.0.10.0", {"start": v(1684.87, 228.6) * mm, "end": v(1684.87, 244.47) * mm});
            skLineSegment(sketch, "E36.3.10.0", {"start": v(1684.87, 228.6) * mm, "end": v(1761.07, 228.6) * mm});
            skLineSegment(sketch, "E36.6.10.0", {"start": v(1684.87, 244.47) * mm, "end": v(1761.07, 244.47) * mm});
            skLineSegment(sketch, "E36.9.10.0", {"start": v(1761.07, 228.6) * mm, "end": v(1761.07, 244.47) * mm});
            skLineSegment(sketch, "E36.0.11.0", {"start": v(1845.73, 228.6) * mm, "end": v(1845.73, 244.47) * mm});
            skLineSegment(sketch, "E36.3.11.0", {"start": v(1845.73, 228.6) * mm, "end": v(1921.93, 228.6) * mm});
            skLineSegment(sketch, "E36.6.11.0", {"start": v(1845.73, 244.47) * mm, "end": v(1921.93, 244.47) * mm});
            skLineSegment(sketch, "E36.9.11.0", {"start": v(1921.93, 228.6) * mm, "end": v(1921.93, 244.47) * mm});
            skLineSegment(sketch, "E37.0.12.0", {"start": v(2006.6, 228.6) * mm, "end": v(2006.6, 244.47) * mm});
            skLineSegment(sketch, "E37.3.12.0", {"start": v(2006.6, 228.6) * mm, "end": v(2082.8, 228.6) * mm});
            skLineSegment(sketch, "E37.6.12.0", {"start": v(2006.6, 244.47) * mm, "end": v(2082.8, 244.47) * mm});
            skLineSegment(sketch, "E37.9.12.0", {"start": v(2082.8, 228.6) * mm, "end": v(2082.8, 244.47) * mm});
            skSolve(sketch);
        }
        {
            var Q0;
            Q0 = qSketchRegion(id + "F20", true);
            var Q1;
            Q1=makeQuery(id+"F4.opExtrude","SWEPT_FACE",FACE,{"disambiguationData":[OSD([sQuery(id+"F3.wireOp",EDGE,"E6.right")])]});
            extrude(context, id + "F21", {"entities" : qUnion([Q0]), "endBound" : BoundingType.UP_TO_SURFACE, "depth" : 25.4 * mm, "endBoundEntityFace" : qUnion([Q1]), "offsetDistance" : 25.4 * mm});
        }
        {
            var Q0;
            Q0=makeQuery(id+"F21.opExtrude","SWEPT_FACE",FACE,{"disambiguationData":[OSD([sQuery(id+"F20.wireOp",EDGE,"E37.6.12.0")])]});
            var sketch = newSketch(context, id + "F22", { "sketchPlane" : qUnion([Q0])});
            skCircle(sketch, "E38", {"center": v(63.5, 2044.7) * mm, "radius": 4.76 * mm});
            skLineSegment(sketch, "E39", {"start": v(50.8, 2044.7) * mm, "end": v(63.5, 2044.7) * mm, "construction": true});
            skLineSegment(sketch, "E40", {"start": v(76.2, 2044.7) * mm, "end": v(63.5, 2044.7) * mm, "construction": true});
            skCircle(sketch, "E41.0.1.0", {"center": v(63.5, 1883.83) * mm, "radius": 4.76 * mm});
            skCircle(sketch, "E41.0.2.0", {"center": v(63.5, 1722.97) * mm, "radius": 4.76 * mm});
            skCircle(sketch, "E41.0.3.0", {"center": v(63.5, 1562.1) * mm, "radius": 4.76 * mm});
            skCircle(sketch, "E41.0.4.0", {"center": v(63.5, 1401.23) * mm, "radius": 4.76 * mm});
            skCircle(sketch, "E41.0.5.0", {"center": v(63.5, 1240.37) * mm, "radius": 4.76 * mm});
            skCircle(sketch, "E41.0.6.0", {"center": v(63.5, 1079.5) * mm, "radius": 4.76 * mm});
            skCircle(sketch, "E41.0.7.0", {"center": v(63.5, 918.63) * mm, "radius": 4.76 * mm});
            skCircle(sketch, "E41.0.8.0", {"center": v(63.5, 757.77) * mm, "radius": 4.76 * mm});
            skCircle(sketch, "E41.0.9.0", {"center": v(63.5, 596.9) * mm, "radius": 4.76 * mm});
            skCircle(sketch, "E41.0.10.0", {"center": v(63.5, 436.03) * mm, "radius": 4.76 * mm});
            skCircle(sketch, "E41.0.11.0", {"center": v(63.5, 275.17) * mm, "radius": 4.76 * mm});
            skCircle(sketch, "E41.0.12.0", {"center": v(63.5, 114.3) * mm, "radius": 4.76 * mm});
            skCircle(sketch, "E41.1.0.0", {"center": v(1587.5, 2044.7) * mm, "radius": 4.76 * mm});
            skCircle(sketch, "E41.1.1.0", {"center": v(1587.5, 1883.83) * mm, "radius": 4.76 * mm});
            skCircle(sketch, "E41.1.2.0", {"center": v(1587.5, 1722.97) * mm, "radius": 4.76 * mm});
            skCircle(sketch, "E41.1.3.0", {"center": v(1587.5, 1562.1) * mm, "radius": 4.76 * mm});
            skCircle(sketch, "E41.1.4.0", {"center": v(1587.5, 1401.23) * mm, "radius": 4.76 * mm});
            skCircle(sketch, "E41.1.5.0", {"center": v(1587.5, 1240.37) * mm, "radius": 4.76 * mm});
            skCircle(sketch, "E41.1.6.0", {"center": v(1587.5, 1079.5) * mm, "radius": 4.76 * mm});
            skCircle(sketch, "E41.1.7.0", {"center": v(1587.5, 918.63) * mm, "radius": 4.76 * mm});
            skCircle(sketch, "E41.1.8.0", {"center": v(1587.5, 757.77) * mm, "radius": 4.76 * mm});
            skCircle(sketch, "E41.1.9.0", {"center": v(1587.5, 596.9) * mm, "radius": 4.76 * mm});
            skCircle(sketch, "E41.1.10.0", {"center": v(1587.5, 436.03) * mm, "radius": 4.76 * mm});
            skCircle(sketch, "E41.1.11.0", {"center": v(1587.5, 275.17) * mm, "radius": 4.76 * mm});
            skCircle(sketch, "E41.1.12.0", {"center": v(1587.5, 114.3) * mm, "radius": 4.76 * mm});
            skLineSegment(sketch, "E41.direction1", {"start": v(63.5, 2044.7) * mm, "end": v(1587.5, 2044.7) * mm, "construction": true});
            skLineSegment(sketch, "E41.direction2", {"start": v(63.5, 1883.83) * mm, "end": v(63.5, 2044.7) * mm, "construction": true});
            skLineSegment(sketch, "E42", {"start": v(1600.2, 114.3) * mm, "end": v(1587.5, 114.3) * mm, "construction": true});
            skSolve(sketch);
        }
        {
            var Q0;
            Q0 = qSketchRegion(id + "F22", true);
            extrude(context, id + "F23", {"entities" : qUnion([Q0]), "operationType" : NewBodyOperationType.REMOVE, "oppositeDirection" : true, "depth" : 50.8 * mm, "offsetDistance" : 25.4 * mm});
        }
        {
            var Q0;
            Q0=makeQuery(id+"F1.opExtrude","CAP_FACE",FACE,{"disambiguationData":[OSD([sQuery(id+"F0.wireOp",EDGE,"E0.bottom"),sQuery(id+"F0.wireOp",EDGE,"E0.top"),sQuery(id+"F0.wireOp",EDGE,"E0.left"),sQuery(id+"F0.wireOp",EDGE,"E0.right")])],"isStart":true});
            var Q1;
            Q1=makeQuery(id+"F1.opExtrude","CAP_FACE",FACE,{"disambiguationData":[OSD([sQuery(id+"F0.wireOp",EDGE,"E1.bottom"),sQuery(id+"F0.wireOp",EDGE,"E1.top"),sQuery(id+"F0.wireOp",EDGE,"E1.left"),sQuery(id+"F0.wireOp",EDGE,"E1.right")])],"isStart":true});
            chamfer(context, id + "F24", {"entities" : qUnion([Q0, Q1]), "chamferType" : ChamferType.TWO_OFFSETS, "width1" : 177.8 * mm, "oppositeDirection" : false, "width2" : 9.52 * mm, "tangentPropagation" : true});
        }
        {
            var Q0;
            Q0=makeQuery(id+"F1.opExtrude","CAP_EDGE",EDGE,{"disambiguationData":[OSD([sQuery(id+"F0.wireOp",EDGE,"E2.bottom")])],"isStart":true});
            var Q1;
            Q1=makeQuery(id+"F1.opExtrude","CAP_EDGE",EDGE,{"disambiguationData":[OSD([sQuery(id+"F0.wireOp",EDGE,"E3.bottom")])],"isStart":true});
            var Q2;
            Q2=makeQuery(id+"F1.opExtrude","CAP_EDGE",EDGE,{"disambiguationData":[OSD([sQuery(id+"F0.wireOp",EDGE,"E2.left")])],"isStart":true});
            var Q3;
            Q3=makeQuery(id+"F1.opExtrude","CAP_EDGE",EDGE,{"disambiguationData":[OSD([sQuery(id+"F0.wireOp",EDGE,"E2.right")])],"isStart":true});
            var Q4;
            Q4=makeQuery(id+"F1.opExtrude","CAP_EDGE",EDGE,{"disambiguationData":[OSD([sQuery(id+"F0.wireOp",EDGE,"E3.left")])],"isStart":true});
            var Q5;
            Q5=makeQuery(id+"F1.opExtrude","CAP_EDGE",EDGE,{"disambiguationData":[OSD([sQuery(id+"F0.wireOp",EDGE,"E3.right")])],"isStart":true});
            chamfer(context, id + "F25", {"entities" : qUnion([Q0, Q1, Q2, Q3, Q4, Q5]), "chamferType" : ChamferType.TWO_OFFSETS, "width1" : 177.8 * mm, "oppositeDirection" : false, "width2" : 9.52 * mm, "tangentPropagation" : true});
        }
        {
            var Q0;
            Q0=makeQuery(id+"F21.opExtrude","SWEPT_FACE",FACE,{"disambiguationData":[OSD([sQuery(id+"F20.wireOp",EDGE,"E35.2.0.2")])]});
            var sketch = newSketch(context, id + "F26", { "sketchPlane" : qUnion([Q0])});
            skLineSegment(sketch, "E43.bottom", {"start": v(1587.5, 2095.5) * mm, "end": v(63.5, 2095.5) * mm});
            skLineSegment(sketch, "E43.top", {"start": v(1587.5, 63.5) * mm, "end": v(63.5, 63.5) * mm});
            skLineSegment(sketch, "E43.left", {"start": v(1587.5, 2095.5) * mm, "end": v(1587.5, 63.5) * mm});
            skLineSegment(sketch, "E43.right", {"start": v(63.5, 2095.5) * mm, "end": v(63.5, 63.5) * mm});
            skLineSegment(sketch, "E44", {"start": v(825.5, 2108.2) * mm, "end": v(825.5, 63.5) * mm, "construction": true});
            skLineSegment(sketch, "E45", {"start": v(825.5, 50.8) * mm, "end": v(825.5, 2095.5) * mm, "construction": true});
            skSolve(sketch);
        }
        {
            var Q0;
            Q0 = qSketchRegion(id + "F26", true);
            extrude(context, id + "F27", {"entities" : qUnion([Q0]), "depth" : 254 * mm, "offsetDistance" : 25.4 * mm});
        }
    });
